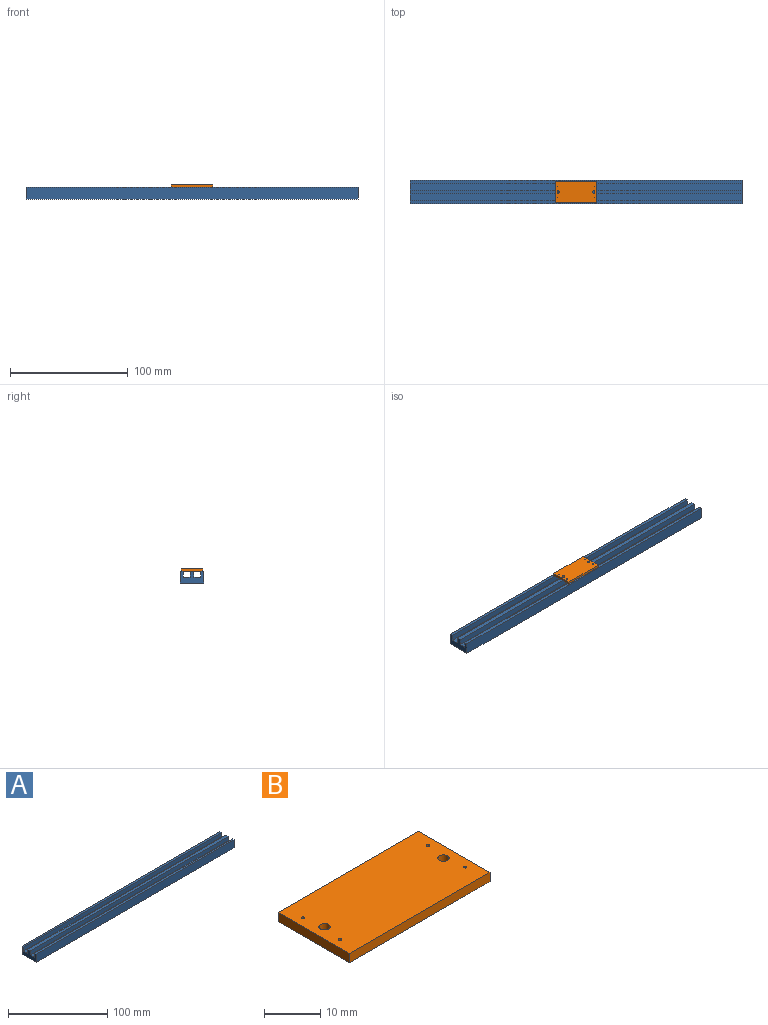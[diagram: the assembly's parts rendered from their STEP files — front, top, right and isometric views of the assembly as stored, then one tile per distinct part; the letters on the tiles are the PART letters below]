
ASSEMBLY  parts=2 mates=1
PART A: 14 faces, bbox 281.8x20x10 mm
  f0: plane 281.8x5.83mm, normal (0,0,1), area 1643.8mm2, adj f2,f4,f9,f12
  f1: plane 281.8x5.83mm, normal (0,0,1), area 1643.8mm2, adj f2,f4,f7,f11
  f2: plane 20x10mm, normal (1,0,0), area 141.7mm2, adj f0,f1,f3,f5,f6,f7,f8,f9
  f3: plane 281.8x10mm, normal (0,1,0), area 2818mm2, adj f2,f4,f6,f8
  f4: plane 20x10mm, normal (-1,0,0), area 141.7mm2, adj f0,f1,f3,f5,f6,f7,f8,f9
  f5: plane 281.8x10mm, normal (0,-1,0), area 2818mm2, adj f2,f4,f6,f10
  f6: plane 281.8x20mm, normal (0,0,-1), area 5636mm2, adj f2,f3,f4,f5
  f7: plane 281.8x5mm, normal (0,-1,0), area 1409mm2, adj f1,f2,f4,f8
  f8: plane 281.8x2.5mm, normal (0,0,1), area 704.5mm2, adj f2,f3,f4,f7
  f9: plane 281.8x5mm, normal (0,1,0), area 1409mm2, adj f0,f2,f4,f10
  f10: plane 281.8x2.5mm, normal (0,0,1), area 704.5mm2, adj f2,f4,f5,f9
  f11: plane 281.8x5mm, normal (0,1,0), area 1409mm2, adj f1,f2,f4,f13
  f12: plane 281.8x5mm, normal (0,-1,0), area 1409mm2, adj f0,f2,f4,f13
  f13: plane 281.8x3.33mm, normal (0,0,1), area 939.3mm2, adj f2,f4,f11,f12
PART B: 12 faces, bbox 35.5x18x2 mm
  f0: plane 18x2mm, normal (1,0,0), area 36mm2, adj f1,f8,f10,f11
  f1: plane 35.5x2mm, normal (0,1,0), area 71mm2, adj f0,f2,f10,f11
  f2: plane 18x2mm, normal (-1,0,0), area 36mm2, adj f1,f8,f10,f11
  f3: cylinder r=0.3mm len=2mm, axis (0,0,-1), area 3.8mm2, adj f10,f11
  f4: cylinder r=0.3mm len=2mm, axis (0,0,-1), area 3.8mm2, adj f10,f11
  f5: cylinder r=1mm len=2mm, axis (0,0,-1), area 12.6mm2, adj f10,f11
  f6: cylinder r=0.3mm len=2mm, axis (0,0,-1), area 3.8mm2, adj f10,f11
  f7: cylinder r=1mm len=2mm, axis (0,0,-1), area 12.6mm2, adj f10,f11
  f8: plane 35.5x2mm, normal (0,-1,0), area 71mm2, adj f0,f2,f10,f11
  f9: cylinder r=0.3mm len=2mm, axis (0,0,-1), area 3.8mm2, adj f10,f11
  f10: plane 35.5x18mm, normal (0,0,1), area 631.6mm2, adj f0,f1,f2,f3,f4,f5,f6,f7
  f11: plane 35.5x18mm, normal (0,0,-1), area 631.6mm2, adj f0,f1,f2,f3,f4,f5,f6,f7
PLACE A t=(-0.5,-0.38,-5.14)mm
PLACE B t=(-0.5,-0.38,4.86)mm
MATE planar B.f11 <-> A.f13  axis (0,0,-1) through (-0.5,-0.38,4.86)mm
